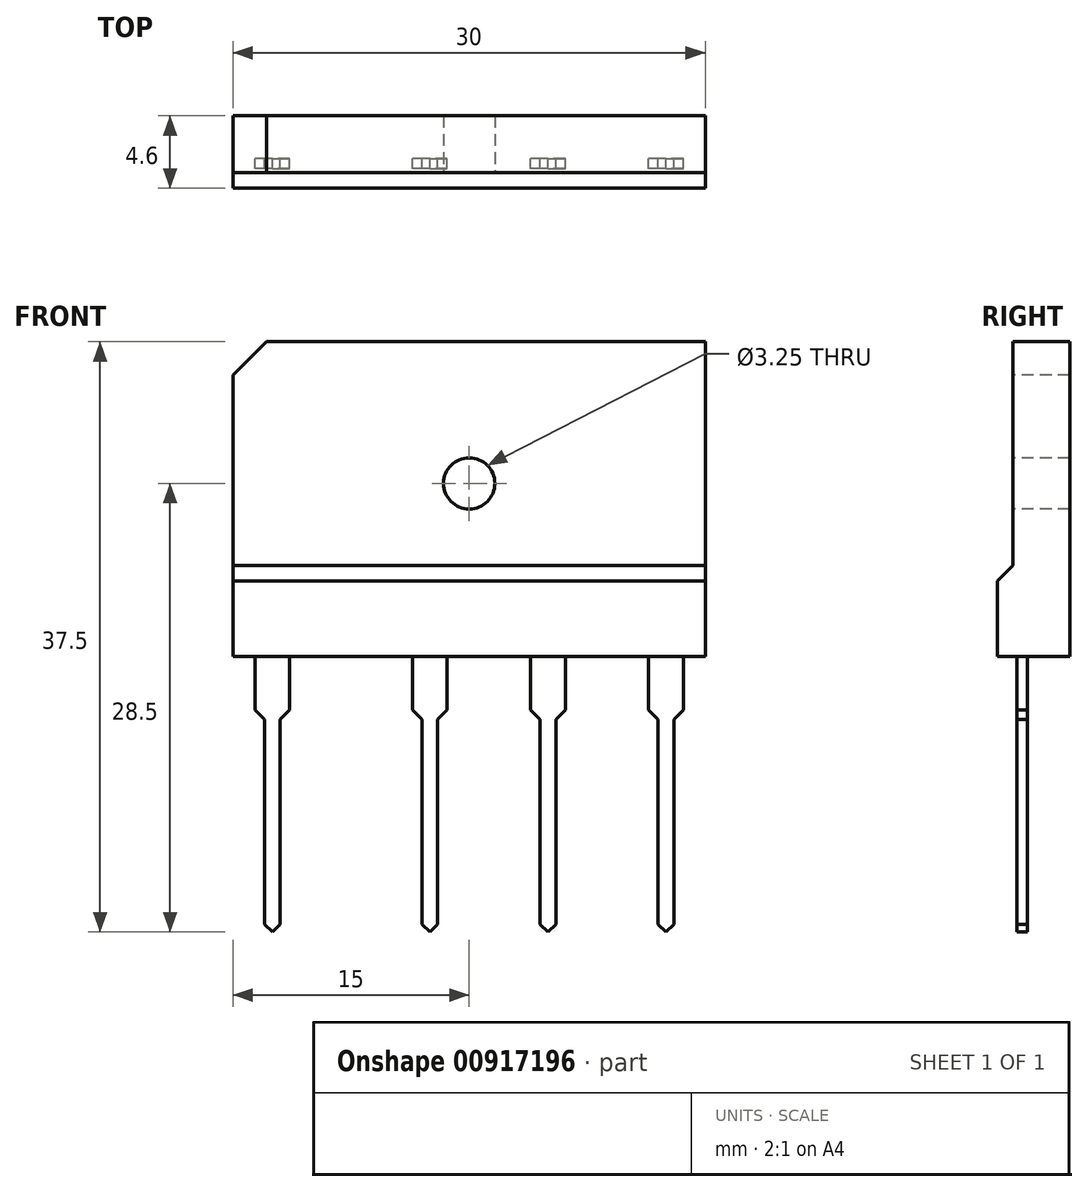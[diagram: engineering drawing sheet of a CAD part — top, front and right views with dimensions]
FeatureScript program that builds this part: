
annotation { "Feature Type Name" : "Feature", "Feature Type Description" : "" }
export const myFeature = defineFeature(function(context is Context, id is Id, definition is map)
    precondition{}
    {
        {
            var Q0;
            Q0=qCreatedBy(makeId("Right.planeOp"),FACE);
            var sketch = newSketch(context, id + "F0", { "sketchPlane" : qUnion([Q0])});
            skLineSegment(sketch, "E0", {"start": v(-0.33, 4) * mm, "end": v(0.32, 4) * mm});
            skLineSegment(sketch, "E1", {"start": v(0.32, 4) * mm, "end": v(3.02, 4) * mm});
            skLineSegment(sketch, "E2", {"start": v(3.02, 4) * mm, "end": v(3.02, 24) * mm});
            skLineSegment(sketch, "E3", {"start": v(3.02, 24) * mm, "end": v(-0.58, 24) * mm});
            skLineSegment(sketch, "E4", {"start": v(-0.58, 24) * mm, "end": v(-0.58, 9.8) * mm});
            skLineSegment(sketch, "E5", {"start": v(-0.57, 9.8) * mm, "end": v(-1.57, 8.8) * mm});
            skLineSegment(sketch, "E6", {"start": v(-1.58, 8.8) * mm, "end": v(-1.58, 4) * mm});
            skLineSegment(sketch, "E7", {"start": v(-1.58, 4) * mm, "end": v(-0.33, 4) * mm});
            skLineSegment(sketch, "E8", {"start": v(0, 0) * mm, "end": v(0, 4) * mm});
            skSolve(sketch);
        }
        {
            var Q0;
            Q0=makeQuery(id+"F0.imprint","IMPRINT",FACE,{"disambiguationData":[TD([[makeQuery(id+"F0.imprint","IMPRINT",EDGE,{"derivedFrom":sQuery(id+"F0.wireOp",EDGE,"E0")}),1.0]])]});
            extrude(context, id + "F1", {"entities" : qUnion([Q0]), "endBound" : BoundingType.SYMMETRIC, "depth" : 30 * mm, "offsetDistance" : 25 * mm});
        }
        {
            var Q0;
            Q0=makeQuery(id+"F1.opExtrude","SWEPT_FACE",FACE,{"disambiguationData":[OSD([sQuery(id+"F0.wireOp",EDGE,"E4")])]});
            var sketch = newSketch(context, id + "F2", { "sketchPlane" : qUnion([Q0])});
            skLineSegment(sketch, "E9", {"start": v(-15, 21.88) * mm, "end": v(-12.88, 24) * mm});
            skLineSegment(sketch, "E10", {"start": v(-15, 21.88) * mm, "end": v(-15, 24) * mm});
            skLineSegment(sketch, "E11", {"start": v(-15, 24) * mm, "end": v(-12.88, 24) * mm});
            skCircle(sketch, "E12", {"center": v(0, 15) * mm, "radius": 1.63 * mm});
            skSolve(sketch);
        }
        {
            var Q0;
            Q0=makeQuery(id+"F2.imprint","IMPRINT",FACE,{"disambiguationData":[TD([[makeQuery(id+"F2.imprint","IMPRINT",EDGE,{"derivedFrom":sQuery(id+"F2.wireOp",EDGE,"E9")}),1.0]])]});
            var Q1;
            Q1=makeQuery(id+"F2.imprint","IMPRINT",FACE,{"disambiguationData":[TD([[makeQuery(id+"F2.imprint","IMPRINT",EDGE,{"derivedFrom":sQuery(id+"F2.wireOp",EDGE,"E12")}),1.0]])]});
            extrude(context, id + "F3", {"entities" : qUnion([Q0, Q1]), "operationType" : NewBodyOperationType.REMOVE, "endBound" : BoundingType.UP_TO_NEXT, "oppositeDirection" : true, "depth" : 25 * mm, "offsetDistance" : 25 * mm});
        }
        {
            var Q0;
            Q0=qCreatedBy(makeId("Front.planeOp"),FACE);
            var sketch = newSketch(context, id + "F4", { "sketchPlane" : qUnion([Q0])});
            skLineSegment(sketch, "E13", {"start": v(-12.5, 4) * mm, "end": v(-12.5, -13.5) * mm, "construction": true});
            skLineSegment(sketch, "E14", {"start": v(-12.5, -13.5) * mm, "end": v(-13, -13) * mm});
            skLineSegment(sketch, "E15", {"start": v(-13, -13) * mm, "end": v(-13, 0) * mm});
            skLineSegment(sketch, "E16", {"start": v(-13, 0) * mm, "end": v(-13.6, 0.6) * mm});
            skLineSegment(sketch, "E17", {"start": v(-13.6, 0.6) * mm, "end": v(-13.6, 4) * mm});
            skLineSegment(sketch, "E18", {"start": v(-13.6, 4) * mm, "end": v(-12.5, 4) * mm});
            skLineSegment(sketch, "E19.MirrorCS", {"start": v(-11.4, 4) * mm, "end": v(-12.5, 4) * mm});
            skLineSegment(sketch, "E20.MirrorCS", {"start": v(-11.4, 0.6) * mm, "end": v(-11.4, 4) * mm});
            skLineSegment(sketch, "E21.MirrorCS", {"start": v(-12, 0) * mm, "end": v(-11.4, 0.6) * mm});
            skLineSegment(sketch, "E22.MirrorCS", {"start": v(-12, -13) * mm, "end": v(-12, 0) * mm});
            skLineSegment(sketch, "E23.MirrorCS", {"start": v(-12.5, -13.5) * mm, "end": v(-12, -13) * mm});
            skLineSegment(sketch, "E24.0", {"start": v(-7.5, 4) * mm, "end": v(-7.5, -13.5) * mm, "construction": true});
            skLineSegment(sketch, "E25.MirrorCS", {"start": v(-2.5, -13.5) * mm, "end": v(-3, -13) * mm});
            skLineSegment(sketch, "E26.MirrorCS", {"start": v(-2, 0) * mm, "end": v(-1.4, 0.6) * mm});
            skLineSegment(sketch, "E27.MirrorCS", {"start": v(-2.5, -13.5) * mm, "end": v(-2, -13) * mm});
            skLineSegment(sketch, "E28.MirrorCS", {"start": v(-3, 0) * mm, "end": v(-3.6, 0.6) * mm});
            skLineSegment(sketch, "E29.MirrorCS", {"start": v(-2, -13) * mm, "end": v(-2, 0) * mm});
            skLineSegment(sketch, "E30.MirrorCS", {"start": v(-3, -13) * mm, "end": v(-3, 0) * mm});
            skLineSegment(sketch, "E31.MirrorCS", {"start": v(-2.5, 4) * mm, "end": v(-2.5, -13.5) * mm, "construction": true});
            skLineSegment(sketch, "E32.MirrorCS", {"start": v(-1.4, 4) * mm, "end": v(-2.5, 4) * mm});
            skLineSegment(sketch, "E33.MirrorCS", {"start": v(-3.6, 4) * mm, "end": v(-2.5, 4) * mm});
            skLineSegment(sketch, "E34.MirrorCS", {"start": v(-1.4, 0.6) * mm, "end": v(-1.4, 4) * mm});
            skLineSegment(sketch, "E35.MirrorCS", {"start": v(-3.6, 0.6) * mm, "end": v(-3.6, 4) * mm});
            skLineSegment(sketch, "E36.0", {"start": v(1.25, 4) * mm, "end": v(1.25, -13.5) * mm, "construction": true});
            skLineSegment(sketch, "E37.MirrorCS", {"start": v(5.5, 0) * mm, "end": v(6.1, 0.6) * mm});
            skLineSegment(sketch, "E38.MirrorCS", {"start": v(5, -13.5) * mm, "end": v(4.5, -13) * mm});
            skLineSegment(sketch, "E39.MirrorCS", {"start": v(4.5, 0) * mm, "end": v(3.9, 0.6) * mm});
            skLineSegment(sketch, "E40.MirrorCS", {"start": v(5, -13.5) * mm, "end": v(5.5, -13) * mm});
            skLineSegment(sketch, "E41.MirrorCS", {"start": v(6.1, 0.6) * mm, "end": v(6.1, 4) * mm});
            skLineSegment(sketch, "E42.MirrorCS", {"start": v(4.5, -13) * mm, "end": v(4.5, 0) * mm});
            skLineSegment(sketch, "E43.MirrorCS", {"start": v(5.5, -13) * mm, "end": v(5.5, 0) * mm});
            skLineSegment(sketch, "E44.MirrorCS", {"start": v(3.9, 0.6) * mm, "end": v(3.9, 4) * mm});
            skLineSegment(sketch, "E45.MirrorCS", {"start": v(5, 4) * mm, "end": v(5, -13.5) * mm, "construction": true});
            skLineSegment(sketch, "E46.MirrorCS", {"start": v(3.9, 4) * mm, "end": v(5, 4) * mm});
            skLineSegment(sketch, "E47.MirrorCS", {"start": v(6.1, 4) * mm, "end": v(5, 4) * mm});
            skLineSegment(sketch, "E48.0", {"start": v(8.75, 4) * mm, "end": v(8.75, -13.5) * mm, "construction": true});
            skLineSegment(sketch, "E49.MirrorCS", {"start": v(12, 0) * mm, "end": v(11.4, 0.6) * mm});
            skLineSegment(sketch, "E50.MirrorCS", {"start": v(12.5, -13.5) * mm, "end": v(13, -13) * mm});
            skLineSegment(sketch, "E51.MirrorCS", {"start": v(13, 0) * mm, "end": v(13.6, 0.6) * mm});
            skLineSegment(sketch, "E52.MirrorCS", {"start": v(12.5, -13.5) * mm, "end": v(12, -13) * mm});
            skLineSegment(sketch, "E53.MirrorCS", {"start": v(13.6, 0.6) * mm, "end": v(13.6, 4) * mm});
            skLineSegment(sketch, "E54.MirrorCS", {"start": v(11.4, 0.6) * mm, "end": v(11.4, 4) * mm});
            skLineSegment(sketch, "E55.MirrorCS", {"start": v(11.4, 4) * mm, "end": v(12.5, 4) * mm});
            skLineSegment(sketch, "E56.MirrorCS", {"start": v(13.6, 4) * mm, "end": v(12.5, 4) * mm});
            skLineSegment(sketch, "E57.MirrorCS", {"start": v(12.5, 4) * mm, "end": v(12.5, -13.5) * mm, "construction": true});
            skLineSegment(sketch, "E58.MirrorCS", {"start": v(12, -13) * mm, "end": v(12, 0) * mm});
            skLineSegment(sketch, "E59.MirrorCS", {"start": v(13, -13) * mm, "end": v(13, 0) * mm});
            skSolve(sketch);
        }
        {
            var Q0;
            Q0=makeQuery(id+"F4.imprint","IMPRINT",FACE,{"disambiguationData":[TD([[makeQuery(id+"F4.imprint","IMPRINT",EDGE,{"derivedFrom":sQuery(id+"F4.wireOp",EDGE,"E49.MirrorCS")}),-1.0]])]});
            var Q1;
            Q1=makeQuery(id+"F4.imprint","IMPRINT",FACE,{"disambiguationData":[TD([[makeQuery(id+"F4.imprint","IMPRINT",EDGE,{"derivedFrom":sQuery(id+"F4.wireOp",EDGE,"E37.MirrorCS")}),1.0]])]});
            var Q2;
            Q2=makeQuery(id+"F4.imprint","IMPRINT",FACE,{"disambiguationData":[TD([[makeQuery(id+"F4.imprint","IMPRINT",EDGE,{"derivedFrom":sQuery(id+"F4.wireOp",EDGE,"E25.MirrorCS")}),-1.0]])]});
            var Q3;
            Q3=makeQuery(id+"F4.imprint","IMPRINT",FACE,{"disambiguationData":[TD([[makeQuery(id+"F4.imprint","IMPRINT",EDGE,{"derivedFrom":sQuery(id+"F4.wireOp",EDGE,"E14")}),-1.0]])]});
            extrude(context, id + "F5", {"entities" : qUnion([Q0, Q1, Q2, Q3]), "endBound" : BoundingType.SYMMETRIC, "depth" : 0.65 * mm, "offsetDistance" : 25 * mm});
        }
    });
